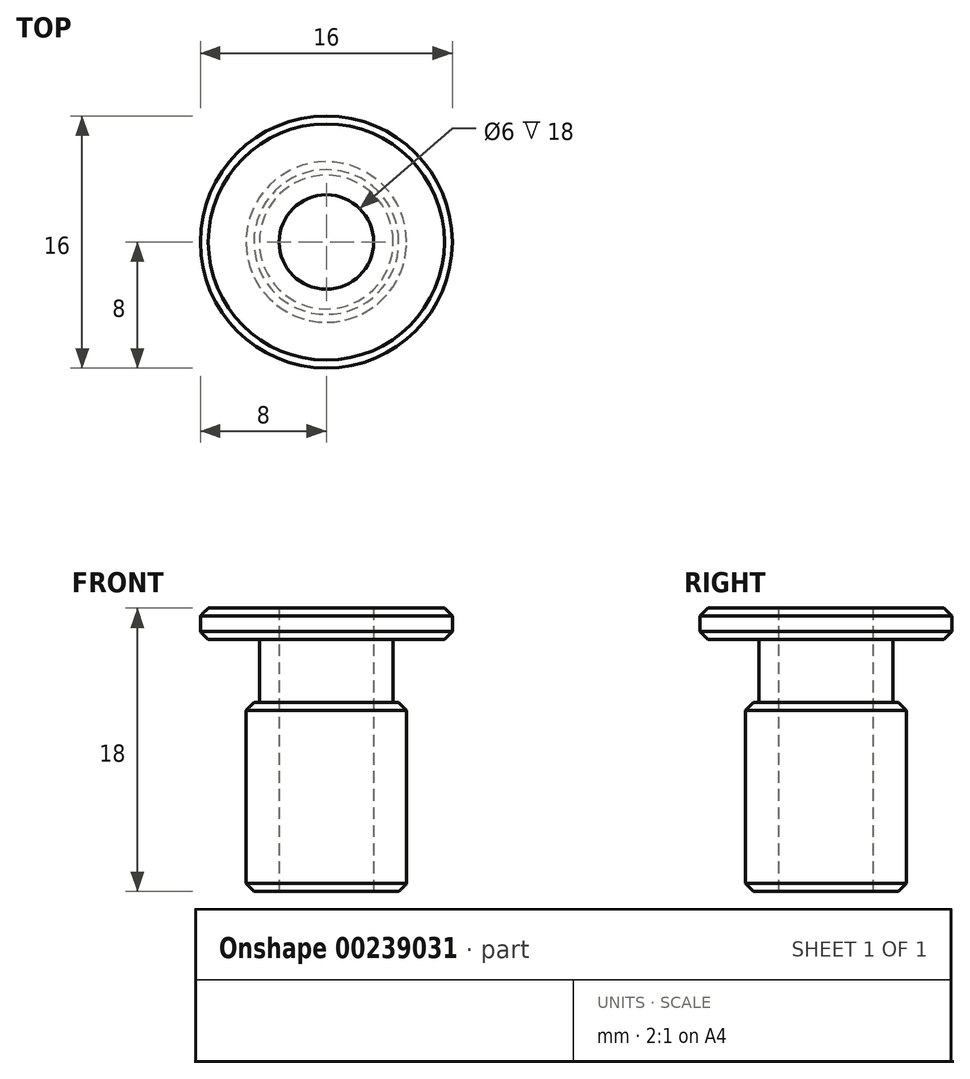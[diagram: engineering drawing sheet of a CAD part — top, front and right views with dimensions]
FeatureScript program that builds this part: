
annotation { "Feature Type Name" : "Feature", "Feature Type Description" : "" }
export const myFeature = defineFeature(function(context is Context, id is Id, definition is map)
    precondition{}
    {
        {
            var Q0;
            Q0=qCreatedBy(makeId("Front.planeOp"),FACE);
            var sketch = newSketch(context, id + "F0", { "sketchPlane" : qUnion([Q0])});
            skLineSegment(sketch, "E0", {"start": v(0, 0) * mm, "end": v(0, 9.32) * mm, "construction": true});
            skLineSegment(sketch, "E1", {"start": v(0, 0) * mm, "end": v(3, 0) * mm});
            skLineSegment(sketch, "E2", {"start": v(3, 0) * mm, "end": v(3, 18) * mm});
            skLineSegment(sketch, "E3", {"start": v(4.25, 16) * mm, "end": v(4.25, 12) * mm});
            skLineSegment(sketch, "E4", {"start": v(4.25, 12) * mm, "end": v(5.1, 12) * mm});
            skLineSegment(sketch, "E5", {"start": v(5.1, 12) * mm, "end": v(5.1, 0) * mm});
            skLineSegment(sketch, "E6", {"start": v(5.1, 0) * mm, "end": v(3, 0) * mm});
            skLineSegment(sketch, "E7", {"start": v(4.25, 16) * mm, "end": v(8, 16) * mm});
            skLineSegment(sketch, "E8", {"start": v(3, 18) * mm, "end": v(8, 18) * mm});
            skLineSegment(sketch, "E9", {"start": v(8, 18) * mm, "end": v(8, 16) * mm});
            skSolve(sketch);
        }
        {
            var Q0;
            Q0=makeQuery(id+"F0.imprint","IMPRINT",FACE,{"disambiguationData":[TD([[makeQuery(id+"F0.imprint","IMPRINT",EDGE,{"derivedFrom":sQuery(id+"F0.wireOp",EDGE,"E2")}),-1.0]])]});
            var Q1;
            Q1=sQuery(id+"F0.wireOp",EDGE,"E0");
            revolve(context, id + "F1", {"entities" : qUnion([Q0]), "axis" : qUnion([Q1]), "revolveType" : RevolveType.FULL});
        }
        {
            var Q0;
            Q0=makeQuery(id+"F1.opRevolve","SWEPT_EDGE",EDGE,{"disambiguationData":[OSD([sQuery(id+"F0.wireOp",EDGE,"E8"),sQuery(id+"F0.wireOp",EDGE,"E9")])]});
            var Q1;
            Q1=makeQuery(id+"F1.opRevolve","SWEPT_EDGE",EDGE,{"disambiguationData":[OSD([sQuery(id+"F0.wireOp",EDGE,"E7"),sQuery(id+"F0.wireOp",EDGE,"E9")])]});
            var Q2;
            Q2=makeQuery(id+"F1.opRevolve","SWEPT_EDGE",EDGE,{"disambiguationData":[OSD([sQuery(id+"F0.wireOp",EDGE,"E4"),sQuery(id+"F0.wireOp",EDGE,"E5")])]});
            var Q3;
            Q3=makeQuery(id+"F1.opRevolve","SWEPT_EDGE",EDGE,{"disambiguationData":[OSD([sQuery(id+"F0.wireOp",EDGE,"E5"),sQuery(id+"F0.wireOp",EDGE,"E6")])]});
            chamfer(context, id + "F2", {"entities" : qUnion([Q0, Q1, Q2, Q3]), "chamferType" : ChamferType.OFFSET_ANGLE, "width" : .5 * mm, "oppositeDirection" : false, "angle" : 45 * degree, "tangentPropagation" : true});
        }
    });
